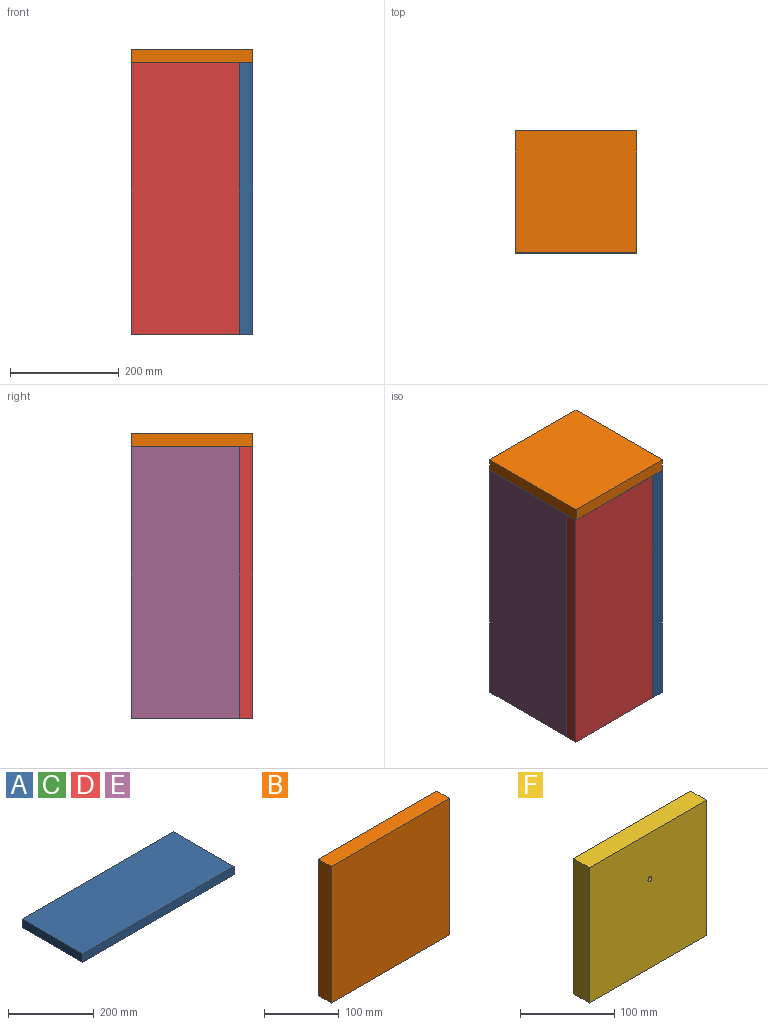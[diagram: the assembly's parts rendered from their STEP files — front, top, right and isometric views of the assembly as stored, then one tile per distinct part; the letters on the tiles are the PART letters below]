
ASSEMBLY  parts=6 mates=5
PART A: 6 faces, bbox 500x200x24 mm
  f0: plane 500x24mm, normal (0,1,0), area 12000mm2, adj f1,f3,f4,f5
  f1: plane 200x24mm, normal (-1,0,0), area 4800mm2, adj f0,f2,f4,f5
  f2: plane 500x24mm, normal (0,-1,0), area 12000mm2, adj f1,f3,f4,f5
  f3: plane 200x24mm, normal (1,0,0), area 4800mm2, adj f0,f2,f4,f5
  f4: plane 500x200mm, normal (0,0,1), area 100000mm2, adj f0,f1,f2,f3
  f5: plane 500x200mm, normal (0,0,-1), area 100000mm2, adj f0,f1,f2,f3
PART B: 6 faces, bbox 224x24x224 mm
  f0: plane 224x24mm, normal (0,0,1), area 5376mm2, adj f1,f3,f4,f5
  f1: plane 224x24mm, normal (-1,0,0), area 5376mm2, adj f0,f2,f4,f5
  f2: plane 224x24mm, normal (0,0,-1), area 5376mm2, adj f1,f3,f4,f5
  f3: plane 224x24mm, normal (1,0,0), area 5376mm2, adj f0,f2,f4,f5
  f4: plane 224x224mm, normal (0,-1,0), area 50176mm2, adj f0,f1,f2,f3
  f5: plane 224x224mm, normal (0,1,0), area 50176mm2, adj f0,f1,f2,f3
PART C: same geometry as A
PART D: same geometry as A
PART E: same geometry as A
PART F: 7 faces, bbox 176x24x176 mm
  f0: plane 176x24mm, normal (0,0,1), area 4224mm2, adj f1,f3,f4,f5
  f1: plane 176x24mm, normal (-1,0,0), area 4224mm2, adj f0,f2,f4,f5
  f2: plane 176x24mm, normal (0,0,-1), area 4224mm2, adj f1,f3,f4,f5
  f3: plane 176x24mm, normal (1,0,0), area 4224mm2, adj f0,f2,f4,f5
  f4: plane 176x176mm, normal (0,1,0), area 30947.7mm2, adj f0,f1,f2,f3,f6
  f5: plane 176x176mm, normal (0,-1,0), area 30947.7mm2, adj f0,f1,f2,f3,f6
  f6: cylinder r=3mm len=24mm, axis (0,-1,0), area 452.4mm2, adj f4,f5
PLACE A rot(axis=(0,1,0),90deg) t=(310.55,-580.06,-366.74)mm
PLACE B rot(axis=(0.58,-0.58,-0.58),120deg) t=(332.52,-638.71,308.92)mm
PLACE C rot(axis=(0.58,0.58,-0.58),120deg) t=(396.25,-617.76,-366.74)mm
PLACE D rot(axis=(-0.58,0.58,0.58),120deg) t=(48.85,-841.76,-366.74)mm
PLACE E rot(axis=(0.71,0,-0.71),180deg) t=(134.55,-879.45,-366.74)mm
PLACE F rot(axis=(-0.58,0.58,-0.58),120deg) t=(190.22,-747.6,-191.08)mm
MATE fastened A.f1 <-> B.f4  axis (0,0,1) through (334.55,-841.76,284.92)mm
MATE fastened D.f2 <-> A.f5  axis (1,0,0) through (310.55,-841.76,34.92)mm
MATE fastened A.f0 <-> C.f4  axis (0,1,0) through (334.55,-641.76,34.92)mm
MATE fastened E.f5 <-> F.f2  axis (1,0,0) through (134.55,-817.76,-215.08)mm
MATE fastened D.f4 <-> E.f0  axis (0,1,0) through (110.55,-817.76,34.92)mm
